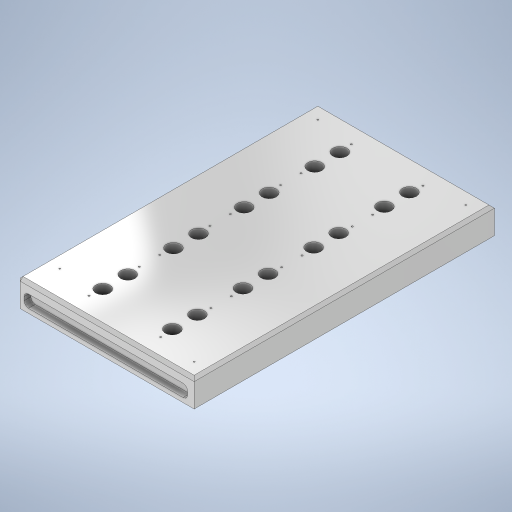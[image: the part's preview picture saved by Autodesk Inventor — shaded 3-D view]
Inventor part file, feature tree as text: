
AUTODESK INVENTOR PART (.ipt)
format: ipt  version: 2023 (Build 270158000, 158)  size: 464,384 bytes
history: native  units: in
note: dims shown in document units (in); Inventor stores cm internally (conversion verified against a paired STEP export)
features: sketch x7, extrude x4, hole x3, chamfer x1
ambient origin geometry x8: Origin, YZ Plane, XZ Plane, XY Plane, X Axis, Y Axis, Z Axis, Center Point
bodies: Solid1 (feature_tree)
feature tree (15):
  extrude  "Extrusion1"  Depth=8.5in
  hole  "Hole3"  [1 undecoded]
  hole  "Hole4"  [1 undecoded]
  extrude  "Extrusion4"  Depth=0.4075in
  extrude  "Extrusion5"  Depth=0.4075in
  hole  "Hole5"  [1 undecoded]
  chamfer  "Chamfer3"  Distance=2.0276in
  extrude  "Extrusion6"  Depth=0.5in
  sketch  "Sketch1"  dims[d0=5.0in d1=8.5in]
  sketch  "Sketch5"  dims[d2=0.75in d3=0.0in d31=0.7894in]
  sketch  "Sketch6"  dims[d32=0.4075in d33=0.4075in]
  sketch  "Sketch8"  dims[d34=0.4075in d35=0.4075in]
  sketch  "Sketch10"  dims[d38=0.4075in]
  sketch  "Sketch11"  dims[d39=0.0402in d40=0.094in d41=0.119in d42=0.0787in d43=0.5635in d44=0.315in d45=0.8108in d46=1.4213in d47=2.0276in d48=0.5394in d49=1.4862in d50=1.5748in d52=2.0in d53=0.3937in d55=0.3937in d57=0.0465in d58=0.12in d59=0.1575in d60=0.0787in d61=90.0deg d62=0.315in d63=0.8108in d77=0.35in d78=0.1875in d79=0.1875in d80=0.125in d81=0.1875in d82=0.0in d83=0.125in d84=0.35in d88=0.125in d89=0.125in d91=0.1875in d92=0.0in d93=0.1875in d94=0.1875in d95=1.5157in d96=0.898in d97=0.7087in d98=1.5157in d99=0.156in d100=0.38in d101=0.4in d102=0.61in d103=0.5635in d104=1.0in d105=0.8108in d106=1.5748in d108=2.0in d109=0.3937in d111=0.3937in d113=0.0787in d114=0.0787in d115=45.0deg d116=0.3937in d117=0.3937in d118=0.3937in d119=0.315in d120=0.315in d121=0.315in d122=0.315in d123=0.3937in d124=0.0787in d125=0.5in d126=0.0in]
  sketch  "Sketch9"  dims[d36=0.4075in d37=0.4075in]
note: 3 required parameter values undecoded (feature->parameter linkage not recoverable at this tier; creation-order binding heuristic only, values carry confidence <= 0.55)
